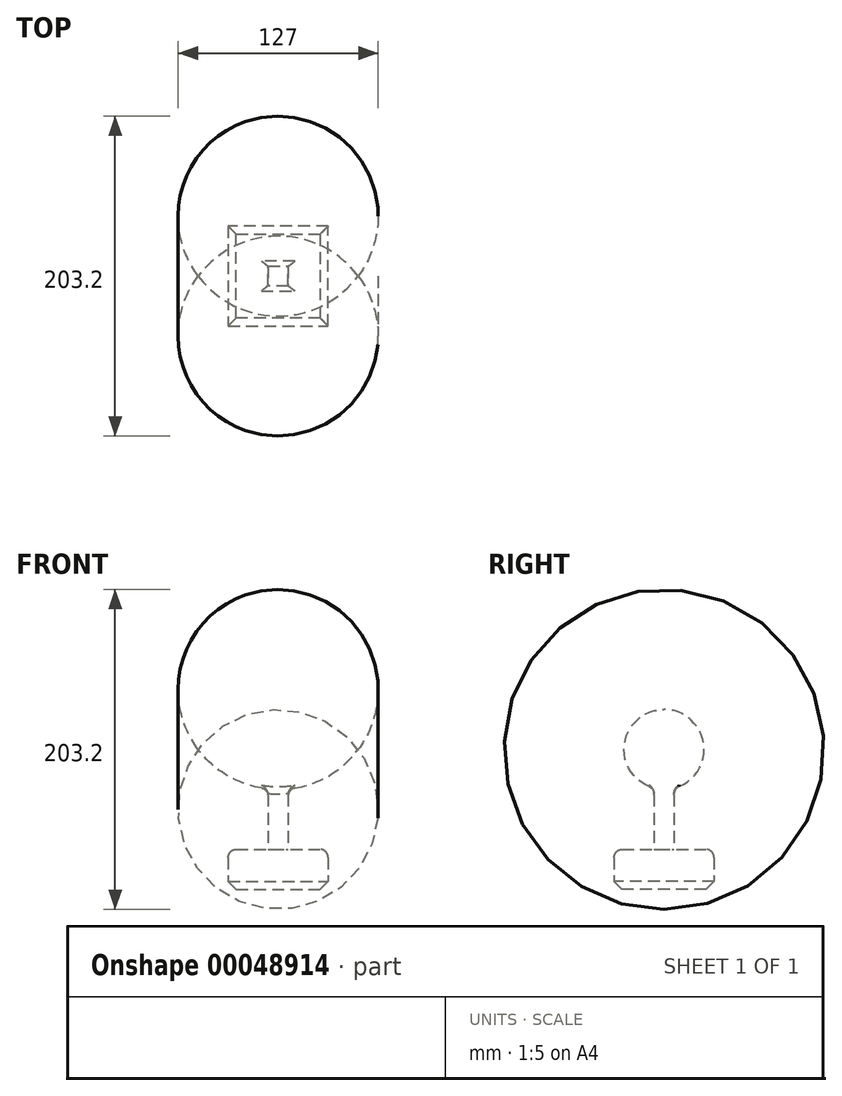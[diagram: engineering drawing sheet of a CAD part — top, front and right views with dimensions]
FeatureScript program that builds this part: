
annotation { "Feature Type Name" : "Feature", "Feature Type Description" : "" }
export const myFeature = defineFeature(function(context is Context, id is Id, definition is map)
    precondition{}
    {
        {
            var Q0;
            Q0=qCreatedBy(makeId("Top.planeOp"),FACE);
            var sketch = newSketch(context, id + "F0", { "sketchPlane" : qUnion([Q0])});
            skLineSegment(sketch, "E0.bottom", {"start": v(0, 0) * mm, "end": v(63.5, 0) * mm});
            skLineSegment(sketch, "E0.top", {"start": v(0, 63.5) * mm, "end": v(63.5, 63.5) * mm});
            skLineSegment(sketch, "E0.left", {"start": v(0, 0) * mm, "end": v(0, 63.5) * mm});
            skLineSegment(sketch, "E0.right", {"start": v(63.5, 0) * mm, "end": v(63.5, 63.5) * mm});
            skSolve(sketch);
        }
        {
            var Q0;
            Q0 = qSketchRegion(id + "F0", true);
            extrude(context, id + "F1", {"entities" : qUnion([Q0]), "depth" : 25.4 * mm});
        }
        {
            var Q0;
            Q0=makeQuery(id+"F1.opExtrude","CAP_FACE",FACE,{"disambiguationData":[OSD([sQuery(id+"F0.wireOp",EDGE,"E0.bottom"),sQuery(id+"F0.wireOp",EDGE,"E0.top"),sQuery(id+"F0.wireOp",EDGE,"E0.left"),sQuery(id+"F0.wireOp",EDGE,"E0.right")])],"isStart":false});
            var sketch = newSketch(context, id + "F2", { "sketchPlane" : qUnion([Q0])});
            skLineSegment(sketch, "E1.0", {"start": v(0, 0) * mm, "end": v(0, 63.5) * mm});
            skLineSegment(sketch, "E1.1", {"start": v(0, 63.5) * mm, "end": v(63.5, 63.5) * mm});
            skLineSegment(sketch, "E1.2", {"start": v(63.5, 0) * mm, "end": v(63.5, 63.5) * mm});
            skLineSegment(sketch, "E1.3", {"start": v(0, 0) * mm, "end": v(63.5, 0) * mm});
            skPoint(sketch, "E2.endSnap0", {"position": v(0, 31.75) * mm});
            skLineSegment(sketch, "E3", {"start": v(31.75, 38.1) * mm, "end": v(38.1, 38.1) * mm});
            skLineSegment(sketch, "E4", {"start": v(38.1, 38.1) * mm, "end": v(38.1, 25.4) * mm});
            skLineSegment(sketch, "E5", {"start": v(38.1, 25.4) * mm, "end": v(25.4, 25.4) * mm});
            skLineSegment(sketch, "E6", {"start": v(25.4, 25.4) * mm, "end": v(25.4, 38.1) * mm});
            skLineSegment(sketch, "E7", {"start": v(25.4, 38.1) * mm, "end": v(31.75, 38.1) * mm});
            skSolve(sketch);
        }
        {
            var Q0;
            Q0=makeQuery(id+"F2.imprint","IMPRINT",FACE,{"disambiguationData":[TD([[makeQuery(id+"F2.imprint","IMPRINT",EDGE,{"derivedFrom":sQuery(id+"F2.wireOp",EDGE,"E3")}),-1.0]])]});
            extrude(context, id + "F3", {"entities" : qUnion([Q0]), "operationType" : NewBodyOperationType.ADD, "depth" : 63.5 * mm});
        }
        {
            var Q0;
            Q0=makeQuery(id+"F3.opExtrude","CAP_FACE",FACE,{"disambiguationData":[OSD([sQuery(id+"F2.wireOp",EDGE,"E3"),sQuery(id+"F2.wireOp",EDGE,"E4"),sQuery(id+"F2.wireOp",EDGE,"E5"),sQuery(id+"F2.wireOp",EDGE,"E6"),sQuery(id+"F2.wireOp",EDGE,"E7")])],"isStart":false});
            var sketch = newSketch(context, id + "F4", { "sketchPlane" : qUnion([Q0])});
            skPoint(sketch, "E8.endSnap0", {"position": v(31.75, 38.1) * mm});
            skLineSegment(sketch, "E9", {"start": v(31.75, 31.75) * mm, "end": v(82.55, 31.75) * mm});
            skPoint(sketch, "E9.endSnap0", {"position": v(38.1, 31.75) * mm});
            skArc(sketch, "E10", {"start": v(82.55, 31.75) * mm, "mid": v(60.15, 50.45) * mm, "end": v(31.75, 57.15) * mm});
            skArc(sketch, "E11.MirrorCS", {"start": v(-19.05, 31.75) * mm, "mid": v(3.35, 50.45) * mm, "end": v(31.75, 57.15) * mm});
            skArc(sketch, "E12.MirrorCS", {"start": v(82.55, 31.75) * mm, "mid": v(60.15, 13.05) * mm, "end": v(31.75, 6.35) * mm});
            skArc(sketch, "E13.MirrorCS", {"start": v(-19.05, 31.75) * mm, "mid": v(3.35, 13.05) * mm, "end": v(31.75, 6.35) * mm});
            skLineSegment(sketch, "E14", {"start": v(31.75, 31.75) * mm, "end": v(-19.05, 31.75) * mm});
            skSolve(sketch);
        }
        {
            var Q0;
            {var subQ7=sQuery(id+"F4.wireOp",EDGE,"E10");Q0=makeQuery(id+"F4.imprint","IMPRINT",FACE,{"disambiguationData":[TD([[makeQuery(id+"F4.imprint","IMPRINT",EDGE,{"derivedFrom":subQ7}),1.0]])]});}
            var Q1;
            {var subQ3=makeQuery(id+"F3.opExtrude","CAP_EDGE",EDGE,{"disambiguationData":[OSD([sQuery(id+"F2.wireOp",EDGE,"E3"),sQuery(id+"F2.wireOp",EDGE,"E7")])],"isStart":false});Q1=makeQuery(id+"F4.imprint","IMPRINT",FACE,{"disambiguationData":[TD([[makeQuery(id+"F4.imprint","IMPRINT",EDGE,{"derivedFrom":subQ3}),-1.0]])]});}
            var Q2;
            Q2=sQuery(id+"F4.wireOp",EDGE,"E9");
            revolve(context, id + "F5", {"operationType" : NewBodyOperationType.ADD, "entities" : qUnion([Q0, Q1]), "axis" : qUnion([Q2]), "revolveType" : RevolveType.FULL});
        }
        {
            var Q0;
            Q0=makeQuery(id+"F5.boolean.opBoolean","INTERSECT",EDGE,{"derivedFrom":[makeQuery(id+"F3.opExtrude","SWEPT_FACE",FACE,{"disambiguationData":[OSD([sQuery(id+"F2.wireOp",EDGE,"E3"),sQuery(id+"F2.wireOp",EDGE,"E7")])]}),makeQuery(id+"F5.opRevolve","SWEPT_FACE",FACE,{"disambiguationData":[OSD([sQuery(id+"F4.wireOp",EDGE,"E10"),sQuery(id+"F4.wireOp",EDGE,"E11.MirrorCS")])]})]});
            var Q1;
            Q1=makeQuery(id+"F5.boolean.opBoolean","INTERSECT",EDGE,{"derivedFrom":[makeQuery(id+"F3.opExtrude","SWEPT_FACE",FACE,{"disambiguationData":[OSD([sQuery(id+"F2.wireOp",EDGE,"E4")])]}),makeQuery(id+"F5.opRevolve","SWEPT_FACE",FACE,{"disambiguationData":[OSD([sQuery(id+"F4.wireOp",EDGE,"E10"),sQuery(id+"F4.wireOp",EDGE,"E11.MirrorCS")])]})]});
            var Q2;
            Q2=makeQuery(id+"F5.boolean.opBoolean","INTERSECT",EDGE,{"derivedFrom":[makeQuery(id+"F3.opExtrude","SWEPT_FACE",FACE,{"disambiguationData":[OSD([sQuery(id+"F2.wireOp",EDGE,"E5")])]}),makeQuery(id+"F5.opRevolve","SWEPT_FACE",FACE,{"disambiguationData":[OSD([sQuery(id+"F4.wireOp",EDGE,"E10"),sQuery(id+"F4.wireOp",EDGE,"E11.MirrorCS")])]})]});
            var Q3;
            Q3=makeQuery(id+"F5.boolean.opBoolean","INTERSECT",EDGE,{"derivedFrom":[makeQuery(id+"F3.opExtrude","SWEPT_FACE",FACE,{"disambiguationData":[OSD([sQuery(id+"F2.wireOp",EDGE,"E6")])]}),makeQuery(id+"F5.opRevolve","SWEPT_FACE",FACE,{"disambiguationData":[OSD([sQuery(id+"F4.wireOp",EDGE,"E10"),sQuery(id+"F4.wireOp",EDGE,"E11.MirrorCS")])]})]});
            var Q4;
            Q4=makeQuery(id+"F1.opExtrude","CAP_EDGE",EDGE,{"disambiguationData":[OSD([sQuery(id+"F0.wireOp",EDGE,"E0.left")])],"isStart":false});
            var Q5;
            Q5=makeQuery(id+"F1.opExtrude","CAP_EDGE",EDGE,{"disambiguationData":[OSD([sQuery(id+"F0.wireOp",EDGE,"E0.bottom")])],"isStart":false});
            var Q6;
            Q6=makeQuery(id+"F1.opExtrude","CAP_EDGE",EDGE,{"disambiguationData":[OSD([sQuery(id+"F0.wireOp",EDGE,"E0.top")])],"isStart":false});
            var Q7;
            Q7=makeQuery(id+"F1.opExtrude","CAP_EDGE",EDGE,{"disambiguationData":[OSD([sQuery(id+"F0.wireOp",EDGE,"E0.right")])],"isStart":false});
            var Q8;
            Q8=makeQuery(id+"F3.opExtrude","CAP_EDGE",EDGE,{"disambiguationData":[OSD([sQuery(id+"F2.wireOp",EDGE,"E6")])],"isStart":true});
            var Q9;
            Q9=makeQuery(id+"F3.opExtrude","CAP_EDGE",EDGE,{"disambiguationData":[OSD([sQuery(id+"F2.wireOp",EDGE,"E5")])],"isStart":true});
            var Q10;
            Q10=makeQuery(id+"F3.opExtrude","CAP_EDGE",EDGE,{"disambiguationData":[OSD([sQuery(id+"F2.wireOp",EDGE,"E3"),sQuery(id+"F2.wireOp",EDGE,"E7")])],"isStart":true});
            var Q11;
            Q11=makeQuery(id+"F3.opExtrude","CAP_EDGE",EDGE,{"disambiguationData":[OSD([sQuery(id+"F2.wireOp",EDGE,"E4")])],"isStart":true});
            fillet(context, id + "F6", {"entities" : qUnion([Q0, Q1, Q2, Q3, Q4, Q5, Q6, Q7, Q8, Q9, Q10, Q11]), "radius" : 5.08 * mm, "tangentPropagation" : true, "allowEdgeOverflow" : false});
        }
        {
            var Q0;
            Q0=makeQuery(id+"F1.opExtrude","CAP_EDGE",EDGE,{"disambiguationData":[OSD([sQuery(id+"F0.wireOp",EDGE,"E0.left")])],"isStart":true});
            var Q1;
            Q1=makeQuery(id+"F1.opExtrude","CAP_EDGE",EDGE,{"disambiguationData":[OSD([sQuery(id+"F0.wireOp",EDGE,"E0.bottom")])],"isStart":true});
            var Q2;
            Q2=makeQuery(id+"F1.opExtrude","CAP_EDGE",EDGE,{"disambiguationData":[OSD([sQuery(id+"F0.wireOp",EDGE,"E0.top")])],"isStart":true});
            var Q3;
            Q3=makeQuery(id+"F1.opExtrude","CAP_EDGE",EDGE,{"disambiguationData":[OSD([sQuery(id+"F0.wireOp",EDGE,"E0.right")])],"isStart":true});
            chamfer(context, id + "F7", {"entities" : qUnion([Q0, Q1, Q2, Q3]), "width" : 5.08 * mm, "tangentPropagation" : true});
        }
    });
